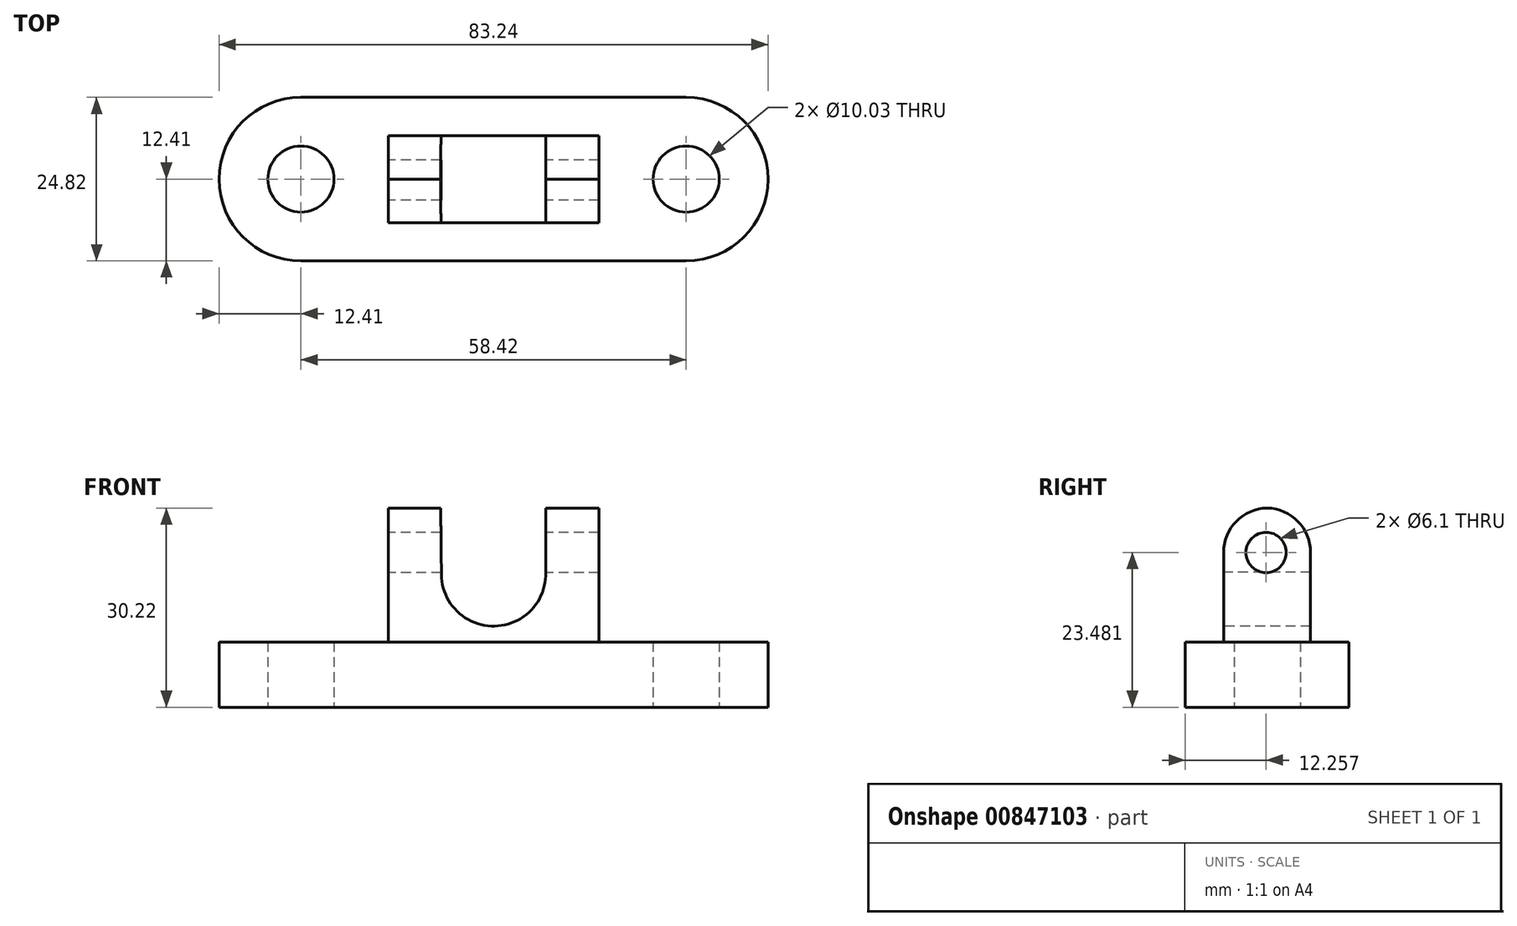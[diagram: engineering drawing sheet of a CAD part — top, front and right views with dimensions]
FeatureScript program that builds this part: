
annotation { "Feature Type Name" : "Feature", "Feature Type Description" : "" }
export const myFeature = defineFeature(function(context is Context, id is Id, definition is map)
    precondition{}
    {
        {
            var Q0;
            Q0=qCreatedBy(makeId("Top.planeOp"),FACE);
            var sketch = newSketch(context, id + "F0", { "sketchPlane" : qUnion([Q0])});
            skLineSegment(sketch, "E0.bottom", {"start": v(29.2, -12.41) * mm, "end": v(-29.2, -12.41) * mm});
            skLineSegment(sketch, "E0.top", {"start": v(29.2, 12.41) * mm, "end": v(-29.2, 12.41) * mm});
            skLineSegment(sketch, "E0.left", {"start": v(29.2, -12.41) * mm, "end": v(29.2, 12.41) * mm});
            skLineSegment(sketch, "E0.right", {"start": v(-29.2, -12.41) * mm, "end": v(-29.2, 12.41) * mm});
            skPoint(sketch, "E0.middle", {"position": v(0, 0) * mm});
            skArc(sketch, "E1", {"start": v(29.2, -12.41) * mm, "mid": v(41.62, 0) * mm, "end": v(29.2, 12.41) * mm});
            skArc(sketch, "E2", {"start": v(-29.21, 12.41) * mm, "mid": v(-41.62, 0) * mm, "end": v(-29.2, -12.41) * mm});
            skCircle(sketch, "E3", {"center": v(-29.2, 0) * mm, "radius": 5.01 * mm});
            skCircle(sketch, "E4", {"center": v(29.2, 0) * mm, "radius": 5.01 * mm});
            skSolve(sketch);
        }
        {
            var Q0;
            {var subQ5=sQuery(id+"F0.wireOp",EDGE,"E0.bottom");Q0=makeQuery(id+"F0.imprint","IMPRINT",FACE,{"disambiguationData":[TD([[makeQuery(id+"F0.imprint","IMPRINT",EDGE,{"derivedFrom":subQ5}),-1.0]])]});}
            var Q1;
            {var subQ0=sQuery(id+"F0.wireOp",EDGE,"E2");Q1=makeQuery(id+"F0.imprint","IMPRINT",FACE,{"disambiguationData":[TD([[makeQuery(id+"F0.imprint","IMPRINT",EDGE,{"derivedFrom":subQ0}),1.0]])]});}
            var Q2;
            {var subQ0=sQuery(id+"F0.wireOp",EDGE,"E1");Q2=makeQuery(id+"F0.imprint","IMPRINT",FACE,{"disambiguationData":[TD([[makeQuery(id+"F0.imprint","IMPRINT",EDGE,{"derivedFrom":subQ0}),1.0]])]});}
            extrude(context, id + "F1", {"entities" : qUnion([Q0, Q1, Q2]), "depth" : 9.9 * mm, "offsetDistance" : 25.4 * mm});
        }
        {
            var Q0;
            Q0=makeQuery(id+"F1.opExtrude","CAP_FACE",FACE,{"disambiguationData":[OSD([sQuery(id+"F0.wireOp",EDGE,"E0.bottom"),sQuery(id+"F0.wireOp",EDGE,"E0.top"),sQuery(id+"F0.wireOp",EDGE,"E1"),sQuery(id+"F0.wireOp",EDGE,"E2"),sQuery(id+"F0.wireOp",EDGE,"E3"),sQuery(id+"F0.wireOp",EDGE,"E4")])],"isStart":false});
            var sketch = newSketch(context, id + "F2", { "sketchPlane" : qUnion([Q0])});
            skLineSegment(sketch, "E5.bottom", {"start": v(15.97, -6.6) * mm, "end": v(-15.97, -6.6) * mm});
            skLineSegment(sketch, "E5.top", {"start": v(15.97, 6.6) * mm, "end": v(-15.97, 6.6) * mm});
            skLineSegment(sketch, "E5.left", {"start": v(15.97, -6.6) * mm, "end": v(15.97, 6.6) * mm});
            skLineSegment(sketch, "E5.right", {"start": v(-15.97, -6.6) * mm, "end": v(-15.97, 6.6) * mm});
            skPoint(sketch, "E5.middle", {"position": v(0, 0) * mm});
            skSolve(sketch);
        }
        {
            var Q0;
            Q0=makeQuery(id+"F2.imprint","IMPRINT",FACE,{"disambiguationData":[TD([[makeQuery(id+"F2.imprint","IMPRINT",EDGE,{"derivedFrom":sQuery(id+"F2.wireOp",EDGE,"E5.bottom")}),-1.0]])]});
            extrude(context, id + "F3", {"entities" : qUnion([Q0]), "operationType" : NewBodyOperationType.ADD, "depth" : 20.32 * mm, "offsetDistance" : 25.4 * mm});
        }
        {
            var Q0;
            Q0=makeQuery(id+"F3.opExtrude","SWEPT_FACE",FACE,{"disambiguationData":[OSD([sQuery(id+"F2.wireOp",EDGE,"E5.bottom")])]});
            var sketch = newSketch(context, id + "F4", { "sketchPlane" : qUnion([Q0])});
            skArc(sketch, "E6", {"start": v(-7.92, 20.14) * mm, "mid": v(0.16, 12.3) * mm, "end": v(7.91, 20.46) * mm});
            skPoint(sketch, "E6.centerSnap0", {"position": v(0, 30.23) * mm});
            skLineSegment(sketch, "E7", {"start": v(-7.92, 20.14) * mm, "end": v(-8.01, 30.23) * mm});
            skLineSegment(sketch, "E8", {"start": v(7.91, 20.46) * mm, "end": v(7.91, 30.23) * mm});
            skSolve(sketch);
        }
        {
            var Q0;
            Q0=makeQuery(id+"F4.imprint","IMPRINT",FACE,{"disambiguationData":[TD([[makeQuery(id+"F4.imprint","IMPRINT",EDGE,{"derivedFrom":sQuery(id+"F4.wireOp",EDGE,"E6")}),1.0]])]});
            extrude(context, id + "F5", {"entities" : qUnion([Q0]), "operationType" : NewBodyOperationType.REMOVE, "oppositeDirection" : true, "depth" : 25.4 * mm, "offsetDistance" : 25.4 * mm});
        }
        {
            var Q0;
            {var subQ0=sQuery(id+"F2.wireOp",EDGE,"E5.bottom");var subQ1=sQuery(id+"F2.wireOp",EDGE,"E5.right");Q0=makeQuery(id+"F5.boolean.opBoolean","SPLIT",EDGE,{"disambiguationData":[TD([makeQuery(id+"F3.opExtrude","SWEPT_FACE",FACE,{"disambiguationData":[OSD([subQ1])]})])],"derivedFrom":makeQuery(id+"F3.opExtrude","CAP_EDGE",EDGE,{"disambiguationData":[OSD([subQ0])],"isStart":false})});}
            var Q1;
            {var subQ0=sQuery(id+"F2.wireOp",EDGE,"E5.right");var subQ1=sQuery(id+"F2.wireOp",EDGE,"E5.top");Q1=makeQuery(id+"F5.boolean.opBoolean","SPLIT",EDGE,{"disambiguationData":[TD([makeQuery(id+"F3.opExtrude","SWEPT_FACE",FACE,{"disambiguationData":[OSD([subQ0])]})])],"derivedFrom":makeQuery(id+"F3.opExtrude","CAP_EDGE",EDGE,{"disambiguationData":[OSD([subQ1])],"isStart":false})});}
            var Q2;
            {var subQ0=sQuery(id+"F2.wireOp",EDGE,"E5.bottom");var subQ1=sQuery(id+"F2.wireOp",EDGE,"E5.left");Q2=makeQuery(id+"F5.boolean.opBoolean","SPLIT",EDGE,{"disambiguationData":[TD([makeQuery(id+"F3.opExtrude","SWEPT_FACE",FACE,{"disambiguationData":[OSD([subQ1])]})])],"derivedFrom":makeQuery(id+"F3.opExtrude","CAP_EDGE",EDGE,{"disambiguationData":[OSD([subQ0])],"isStart":false})});}
            var Q3;
            {var subQ0=sQuery(id+"F2.wireOp",EDGE,"E5.left");var subQ1=sQuery(id+"F2.wireOp",EDGE,"E5.top");Q3=makeQuery(id+"F5.boolean.opBoolean","SPLIT",EDGE,{"disambiguationData":[TD([makeQuery(id+"F3.opExtrude","SWEPT_FACE",FACE,{"disambiguationData":[OSD([subQ0])]})])],"derivedFrom":makeQuery(id+"F3.opExtrude","CAP_EDGE",EDGE,{"disambiguationData":[OSD([subQ1])],"isStart":false})});}
            fillet(context, id + "F6", {"entities" : qUnion([Q0, Q1, Q2, Q3]), "radius" : 6.75 * mm, "tangentPropagation" : true, "allowEdgeOverflow" : false});
        }
        {
            var Q0;
            Q0=makeQuery(id+"F3.opExtrude","SWEPT_FACE",FACE,{"disambiguationData":[OSD([sQuery(id+"F2.wireOp",EDGE,"E5.right")])]});
            var sketch = newSketch(context, id + "F7", { "sketchPlane" : qUnion([Q0])});
            skCircle(sketch, "E9", {"center": v(0.15, 23.48) * mm, "radius": 3.05 * mm});
            skSolve(sketch);
        }
        {
            var Q0;
            Q0=makeQuery(id+"F7.imprint","IMPRINT",FACE,{"disambiguationData":[TD([[makeQuery(id+"F7.imprint","IMPRINT",EDGE,{"derivedFrom":sQuery(id+"F7.wireOp",EDGE,"E9")}),1.0]])]});
            extrude(context, id + "F8", {"entities" : qUnion([Q0]), "operationType" : NewBodyOperationType.REMOVE, "endBound" : BoundingType.THROUGH_ALL, "oppositeDirection" : true, "depth" : 25.4 * mm, "offsetDistance" : 25.4 * mm});
        }
    });
